# Revit family: Curtain_Panel_DORMA_Visur_2-Leaf_manual
name_source: partatom
category: Türen
revit_build: Autodesk Revit 2016 (Build: 20150220_1215(x64)
units: mm (PartAtom-declared; Revit-internal decimal feet)

## family parameters
Beim Laden mit Abzugskörper schneiden = Nein
Gemeinsam genutzt = Nein
Immer vertikal = Ja
OmniClass-Nummer = 23.30.10.00
OmniClass-Titel = Doors
Raumberechnungspunkt = Nein

## types (2) — shared parameters
Analytische Konstruktion = <None>
BIMobject category = Doors
Bauelement = L20
Baugruppenkennzeichen = C1020100
Beschreibung = All-glass double action doors without any visible fixings. Meet VISUR, a system patented for DORMA that secures double-action glass doors without the need for any visually disruptive functional elements. VISUR presents the door in perfect transparency. Rather than cluttering the outline of the leaf, the hardware components are located in the surrounding structures.
COBIe Type Category = Door
Design country = Germany
EAN code = http://-
Edition number = 1
Funktion = Innen
Glazing Material = Glass-Dorma Glazing-Clear
Handle Bar Type = Ironmongery-Door_Closer-Dorma-Visur_Floor_Closer
Handle X = 80 mm  [stored 0.262467 ft]
Hersteller = DORMA
IFC Classification = Door
Ironmongery = Aluminium-Dorma Metal-Anodized Silver
Manufacturer country = Germany
Manufacturer name = DORMA
Material main = Metal
Material secondary = Glass
Modell = DORMA Visur
NBS Reference Code = 36-37-21
NBS Reference Description = Door Hinges
Product SKU = VISUR_001-1
UNSPSC Code = 301715
Uniclass 2.0 Code = PR-36-37-21
_current revision = 1
zero-valued in all types: Barcode, NominalHeight, NominalWidth, Offset, SerialNumber, TagNumber, WarrentyDuration

## per-type parameters (varying)
| type | Dicke | URL |
| Visur Double Door Panel 10mm Glass | 10 mm  [stored 0.0328084 ft] | http://www.dorma-uk.co.uk |
| Visur Double Door Panel 12mm Glass | 12 mm  [stored 0.0393701 ft] | http://www.dorma.com |

note: [stored X ft] marks values corroborated as IEEE doubles in the binary element streams (Revit-internal decimal feet)

## geometry (parser evidence)
native form markers: Blend x4, Sweep x7
no freeform markers — native parametric forms only
